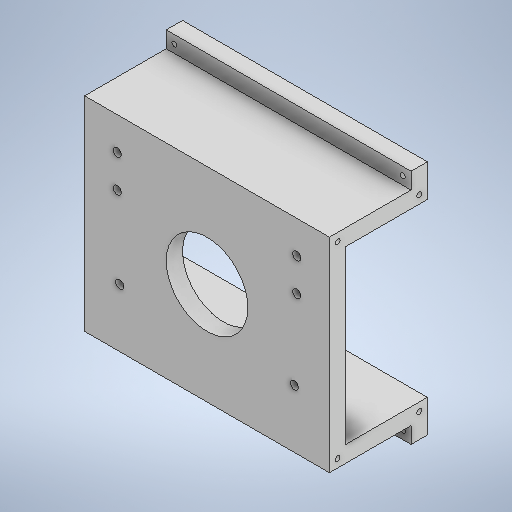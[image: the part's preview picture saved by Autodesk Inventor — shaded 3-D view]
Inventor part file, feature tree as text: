
AUTODESK INVENTOR PART (.ipt)
format: ipt  version: 2025.3 (Build 293356000, 356)  size: 600,576 bytes
history: native  units: mm
features: extrude x6, sketch x3, other x1
ambient origin geometry x8: Origin, YZ Plane, XZ Plane, XY Plane, X Axis, Y Axis, Z Axis, Center Point
bodies: Body1 (feature_tree)
feature tree (10):
  other  "솔리드1"
  sketch  "스케치1"
  extrude  "돌출1"  Depth=150.0mm
  extrude  "돌출2"  Depth=145.0mm
  extrude  "돌출3"  Depth=20.0mm
  extrude  "돌출4"  Depth=20.0mm
  extrude  "돌출5"  Depth=10.0mm TaperAngle=0.0deg
  extrude  "돌출6"  Depth=50.0mm TaperAngle=0.0deg
  sketch  "스케치2"
  sketch  "스케치3"
